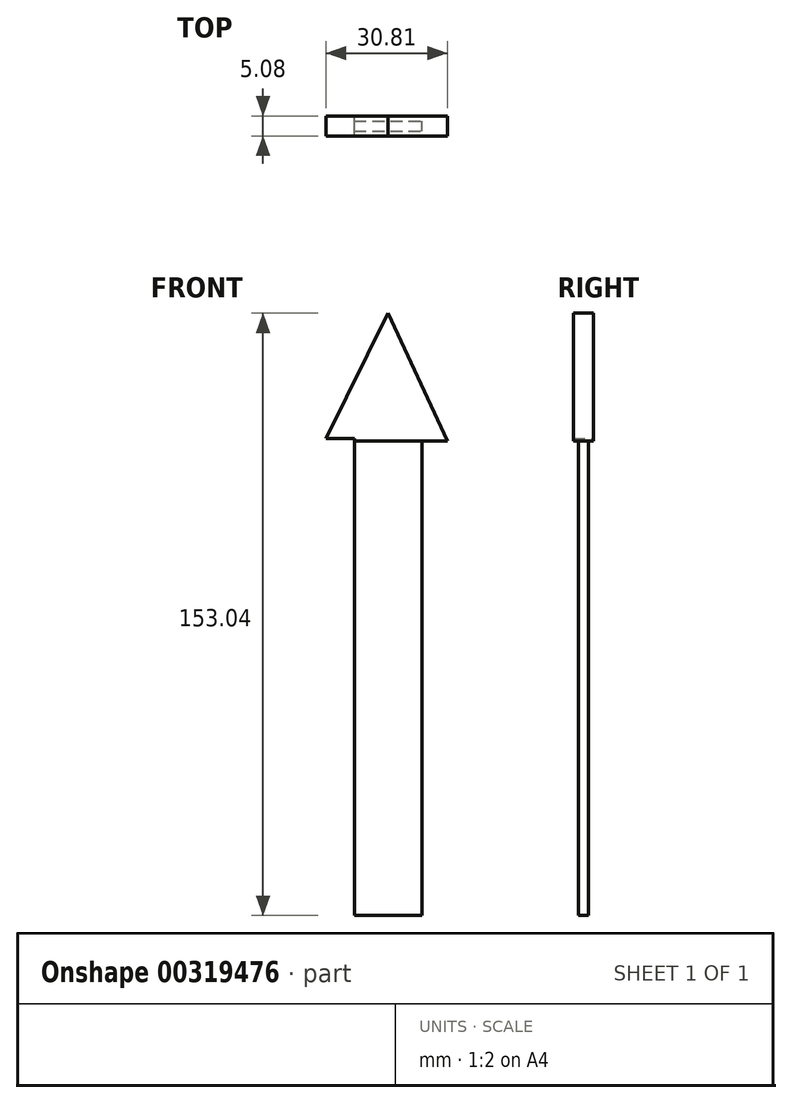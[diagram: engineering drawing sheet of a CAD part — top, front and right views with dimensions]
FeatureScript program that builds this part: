
annotation { "Feature Type Name" : "Feature", "Feature Type Description" : "" }
export const myFeature = defineFeature(function(context is Context, id is Id, definition is map)
    precondition{}
    {
        {
            var Q0;
            Q0=qCreatedBy(makeId("Front.planeOp"),FACE);
            var sketch = newSketch(context, id + "F0", { "sketchPlane" : qUnion([Q0])});
            skLineSegment(sketch, "E0", {"start": v(-13.01, 34.92) * mm, "end": v(-13.01, -86.28) * mm});
            skLineSegment(sketch, "E1", {"start": v(-13.01, -86.28) * mm, "end": v(4.1, -86.28) * mm});
            skLineSegment(sketch, "E2", {"start": v(4.1, -86.28) * mm, "end": v(4.1, 34.24) * mm});
            skLineSegment(sketch, "E3", {"start": v(4.1, 34.24) * mm, "end": v(-13.01, 34.24) * mm});
            skLineSegment(sketch, "E4", {"start": v(-4.45, 34.24) * mm, "end": v(-4.45, -86.28) * mm});
            skLineSegment(sketch, "E5", {"start": v(4.1, 34.24) * mm, "end": v(10.61, 34.24) * mm});
            skLineSegment(sketch, "E6", {"start": v(10.61, 34.24) * mm, "end": v(-4.45, 66.76) * mm});
            skLineSegment(sketch, "E7", {"start": v(-4.45, 66.76) * mm, "end": v(-20.2, 34.92) * mm});
            skLineSegment(sketch, "E8", {"start": v(-20.2, 34.92) * mm, "end": v(-13.01, 34.92) * mm});
            skLineSegment(sketch, "E9", {"start": v(-4.45, 34.24) * mm, "end": v(-4.45, 66.76) * mm});
            skSolve(sketch);
        }
        {
            var Q0;
            {var subQ5=sQuery(id+"F0.wireOp",EDGE,"E4");Q0=makeQuery(id+"F0.imprint","IMPRINT",FACE,{"disambiguationData":[TD([[makeQuery(id+"F0.imprint","IMPRINT",EDGE,{"derivedFrom":subQ5}),-1.0]])]});}
            var Q1;
            {var subQ0=sQuery(id+"F0.wireOp",EDGE,"E2");Q1=makeQuery(id+"F0.imprint","IMPRINT",FACE,{"disambiguationData":[TD([[makeQuery(id+"F0.imprint","IMPRINT",EDGE,{"derivedFrom":subQ0}),1.0]])]});}
            extrude(context, id + "F1", {"entities" : qUnion([Q0, Q1]), "endBound" : BoundingType.SYMMETRIC, "depth" : 2.54 * mm});
        }
        {
            var Q0;
            Q0=makeQuery(id+"F0.imprint","IMPRINT",FACE,{"disambiguationData":[TD([[makeQuery(id+"F0.imprint","IMPRINT",EDGE,{"derivedFrom":sQuery(id+"F0.wireOp",EDGE,"E7")}),1.0]])]});
            var Q1;
            {var subQ0=sQuery(id+"F0.wireOp",EDGE,"E5");Q1=makeQuery(id+"F0.imprint","IMPRINT",FACE,{"disambiguationData":[TD([[makeQuery(id+"F0.imprint","IMPRINT",EDGE,{"derivedFrom":subQ0}),1.0]])]});}
            extrude(context, id + "F2", {"entities" : qUnion([Q0, Q1]), "operationType" : NewBodyOperationType.ADD, "endBound" : BoundingType.SYMMETRIC, "depth" : 5.08 * mm});
        }
    });
